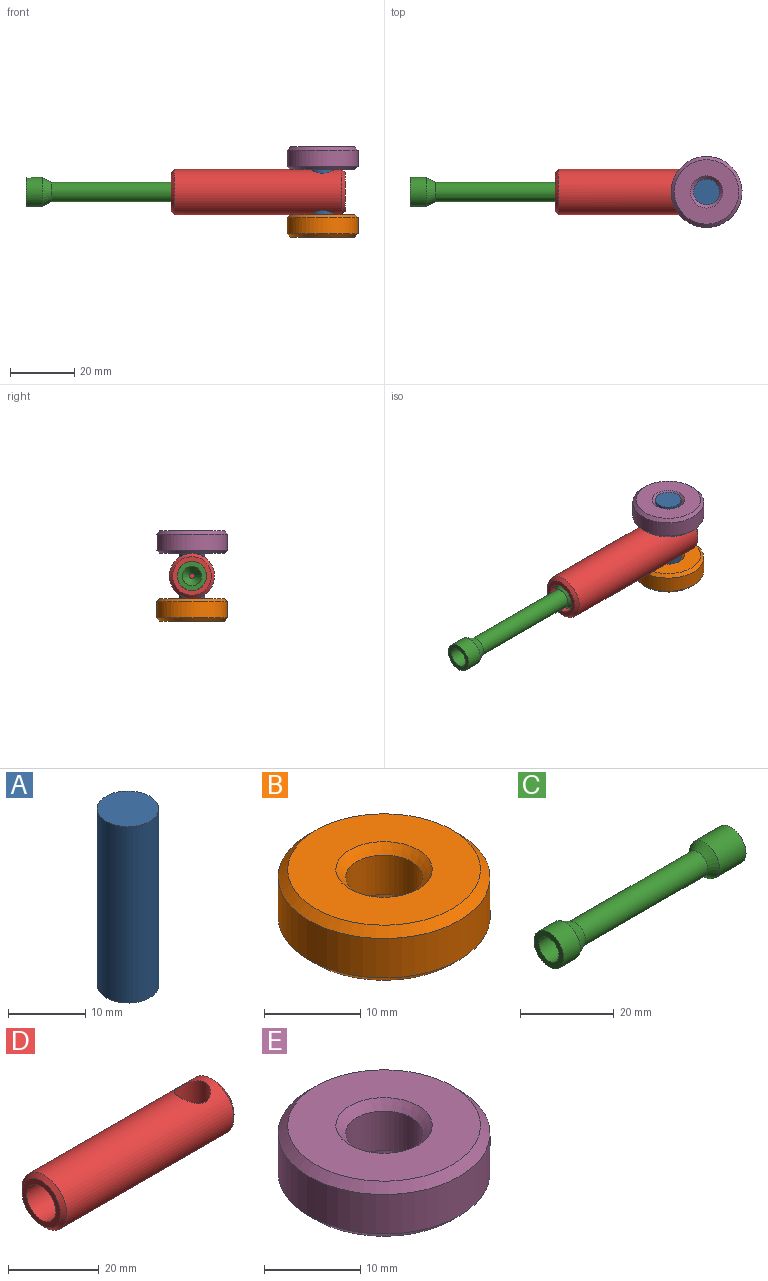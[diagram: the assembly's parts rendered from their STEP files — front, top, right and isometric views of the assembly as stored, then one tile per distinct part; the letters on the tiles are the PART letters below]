
ASSEMBLY  parts=5 mates=4
PART A: 3 faces, bbox 8x8x28 mm
  f0: cylinder r=4mm len=28mm, axis (0,0,1), area 703.7mm2, adj f1,f2
  f1: plane 8x8mm, normal (0,0,-1), area 50.3mm2, adj f0
  f2: plane 8x8mm, normal (0,0,1), area 50.3mm2, adj f0
PART B: 8 faces, bbox 22x22x7 mm
  f0: cylinder r=4mm len=8mm, axis (0,0,1), area 125.7mm2, adj f4,f5
  f1: cylinder r=11mm len=22mm, axis (0,0,1), area 345.6mm2, adj f6,f7
  f2: plane 20x20mm, normal (0,0,-1), area 235.6mm2, adj f5,f7
  f3: plane 20x20mm, normal (0,0,1), area 235.6mm2, adj f4,f6
  f4: cone r=5mm half-angle=45deg, axis (0,0,1), area 40mm2, adj f0,f3
  f5: cone r=4mm half-angle=45deg, axis (0,0,-1), area 40mm2, adj f0,f2
  f6: cone r=11mm half-angle=45deg, axis (0,0,-1), area 93.3mm2, adj f1,f3
  f7: cone r=10mm half-angle=45deg, axis (0,0,1), area 93.3mm2, adj f1,f2
PART C: 10 faces, bbox 55x9x9 mm
  f0: cylinder r=4.5mm len=9mm, axis (1,0,0), area 141.4mm2, adj f2,f6
  f1: cylinder r=3mm len=6mm, axis (1,0,0), area 94.2mm2, adj f2,f7
  f2: plane 9x9mm, normal (-1,0,0), area 35.3mm2, adj f0,f1
  f3: cylinder r=4.5mm len=9mm, axis (-1,0,0), area 226.2mm2, adj f4,f9
  f4: cone r=3mm half-angle=36.9deg, axis (1,0,0), area 58.9mm2, adj f3,f5
  f5: cylinder r=3mm len=37mm, axis (-1,0,0), area 697.4mm2, adj f4,f6
  f6: cone r=4.5mm half-angle=26.6deg, axis (-1,0,0), area 79mm2, adj f0,f5
  f7: cone r=3mm half-angle=36.9deg, axis (-1,0,0), area 44.2mm2, adj f1,f8
  f8: cylinder r=0.75mm len=47mm, axis (-1,0,0), area 221.5mm2, adj f7,f9
  f9: plane 9x9mm, normal (1,0,0), area 61.9mm2, adj f3,f8
PART D: 8 faces, bbox 54x14x14 mm
  f0: cylinder r=7mm len=52mm, axis (-1,0,0), area 2181.9mm2, adj f5,f6,f7
  f1: cylinder r=4.5mm len=40mm, axis (-1,0,0), area 1131mm2, adj f2,f4
  f2: plane 9x9mm, normal (-1,0,0), area 63.6mm2, adj f1
  f3: plane 12x12mm, normal (1,0,0), area 113.1mm2, adj f6
  f4: plane 12x12mm, normal (-1,0,0), area 49.5mm2, adj f1,f7
  f5: cylinder r=4mm len=14mm, axis (0,0,1), area 321.1mm2, adj f0
  f6: cone r=7mm half-angle=45deg, axis (-1,0,0), area 57.8mm2, adj f0,f3
  f7: cone r=6mm half-angle=45deg, axis (1,0,0), area 57.8mm2, adj f0,f4
PART E: 8 faces, bbox 22x22x7 mm
  f0: cylinder r=4mm len=8mm, axis (0,0,-1), area 125.7mm2, adj f4,f5
  f1: cylinder r=11mm len=22mm, axis (0,0,-1), area 345.6mm2, adj f6,f7
  f2: plane 20x20mm, normal (0,0,1), area 235.6mm2, adj f5,f7
  f3: plane 20x20mm, normal (0,0,-1), area 235.6mm2, adj f4,f6
  f4: cone r=5mm half-angle=45deg, axis (0,0,-1), area 40mm2, adj f0,f3
  f5: cone r=4mm half-angle=45deg, axis (0,0,1), area 40mm2, adj f0,f2
  f6: cone r=11mm half-angle=45deg, axis (0,0,1), area 93.3mm2, adj f1,f3
  f7: cone r=10mm half-angle=45deg, axis (0,0,-1), area 93.3mm2, adj f1,f2
PLACE A t=(6.89,11.12,15.86)mm
PLACE B t=(6.89,11.12,15.86)mm
PLACE C t=(-3.11,11.12,15.87)mm
PLACE D t=(6.89,11.12,15.87)mm
PLACE E t=(6.89,11.12,15.86)mm
MATE revolute B.f0 <-> A.f0  axis (0,0,-1) through (95.89,11.12,11.86)mm
MATE fastened A.f0 <-> D.f5  axis (0,0,1) through (95.89,11.12,25.86)mm
MATE slider C.f0 <-> D.f0  axis (-1,0,0) through (58.89,11.12,25.87)mm
MATE revolute E.f0 <-> A.f0  axis (0,0,1) through (95.89,11.12,39.86)mm
